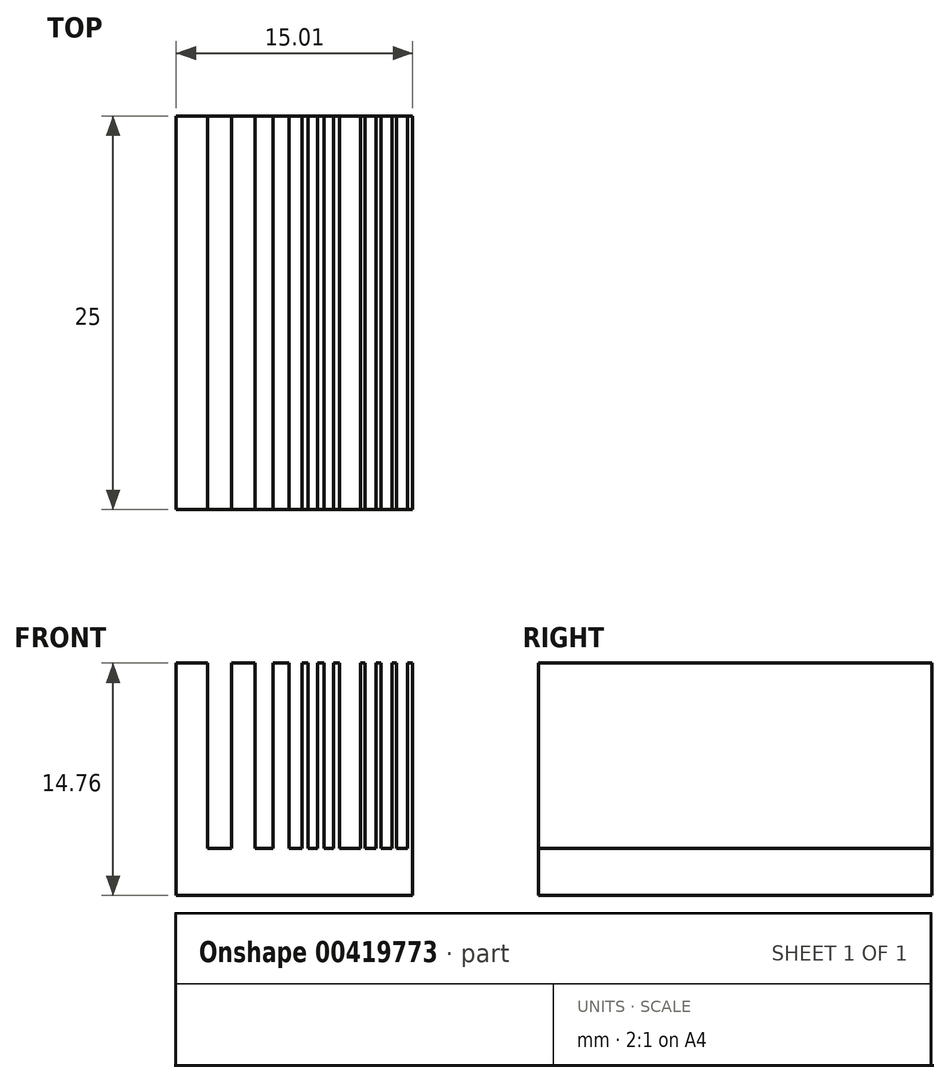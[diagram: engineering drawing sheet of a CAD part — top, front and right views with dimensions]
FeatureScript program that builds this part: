
annotation { "Feature Type Name" : "Feature", "Feature Type Description" : "" }
export const myFeature = defineFeature(function(context is Context, id is Id, definition is map)
    precondition{}
    {
        {
            var Q0;
            Q0=qCreatedBy(makeId("Front.planeOp"),FACE);
            var sketch = newSketch(context, id + "F0", { "sketchPlane" : qUnion([Q0])});
            skLineSegment(sketch, "E0.bottom", {"start": v(-44.62, -17.8) * mm, "end": v(56.98, -17.8) * mm});
            skLineSegment(sketch, "E0.top", {"start": v(-44.62, -22.89) * mm, "end": v(56.98, -22.89) * mm});
            skLineSegment(sketch, "E0.left", {"start": v(-44.62, -17.8) * mm, "end": v(-44.62, -22.89) * mm});
            skLineSegment(sketch, "E0.right", {"start": v(56.98, -17.8) * mm, "end": v(56.98, -22.89) * mm});
            skLineSegment(sketch, "E1.bottom", {"start": v(56.98, -17.8) * mm, "end": v(51.9, -17.8) * mm});
            skLineSegment(sketch, "E1.top", {"start": v(56.98, 7.6) * mm, "end": v(51.9, 7.6) * mm});
            skLineSegment(sketch, "E1.left", {"start": v(56.98, -17.8) * mm, "end": v(56.98, 7.6) * mm});
            skLineSegment(sketch, "E1.right", {"start": v(51.9, -17.8) * mm, "end": v(51.9, 7.6) * mm});
            skLineSegment(sketch, "E2.bottom", {"start": v(-44.62, -17.8) * mm, "end": v(-39.54, -17.8) * mm});
            skLineSegment(sketch, "E2.top", {"start": v(-44.62, 7.6) * mm, "end": v(-39.54, 7.6) * mm});
            skLineSegment(sketch, "E2.left", {"start": v(-44.62, -17.8) * mm, "end": v(-44.62, 7.6) * mm});
            skLineSegment(sketch, "E2.right", {"start": v(-39.54, -17.8) * mm, "end": v(-39.54, 7.6) * mm});
            skLineSegment(sketch, "E3.bottom", {"start": v(-20.37, 7.6) * mm, "end": v(-17.83, 7.6) * mm});
            skLineSegment(sketch, "E3.top", {"start": v(-20.37, -17.8) * mm, "end": v(-17.83, -17.8) * mm});
            skLineSegment(sketch, "E3.left", {"start": v(-20.37, 7.6) * mm, "end": v(-20.37, -17.8) * mm});
            skLineSegment(sketch, "E3.right", {"start": v(-17.83, 7.6) * mm, "end": v(-17.83, -17.8) * mm});
            skLineSegment(sketch, "E4.bottom", {"start": v(3.05, 7.6) * mm, "end": v(8.13, 7.6) * mm});
            skLineSegment(sketch, "E4.top", {"start": v(3.05, -17.8) * mm, "end": v(8.13, -17.8) * mm});
            skLineSegment(sketch, "E4.left", {"start": v(3.05, 7.6) * mm, "end": v(3.05, -17.8) * mm});
            skLineSegment(sketch, "E4.right", {"start": v(8.13, 7.6) * mm, "end": v(8.13, -17.8) * mm});
            skLineSegment(sketch, "E5.bottom", {"start": v(22.11, 7.6) * mm, "end": v(25.92, 7.6) * mm});
            skLineSegment(sketch, "E5.top", {"start": v(22.11, -17.8) * mm, "end": v(25.92, -17.8) * mm});
            skLineSegment(sketch, "E5.left", {"start": v(22.11, 7.6) * mm, "end": v(22.11, -17.8) * mm});
            skLineSegment(sketch, "E5.right", {"start": v(25.92, 7.6) * mm, "end": v(25.92, -17.8) * mm});
            skLineSegment(sketch, "E6.bottom", {"start": v(38.11, 7.6) * mm, "end": v(40.65, 7.6) * mm});
            skLineSegment(sketch, "E6.top", {"start": v(38.11, -17.8) * mm, "end": v(40.65, -17.8) * mm});
            skLineSegment(sketch, "E6.left", {"start": v(38.11, 7.6) * mm, "end": v(38.11, -17.8) * mm});
            skLineSegment(sketch, "E6.right", {"start": v(40.65, 7.6) * mm, "end": v(40.65, -17.8) * mm});
            skLineSegment(sketch, "E7.bottom", {"start": v(-31.28, 7.6) * mm, "end": v(-27.47, 7.6) * mm});
            skLineSegment(sketch, "E7.top", {"start": v(-31.28, -17.8) * mm, "end": v(-27.47, -17.8) * mm});
            skLineSegment(sketch, "E7.left", {"start": v(-31.28, 7.6) * mm, "end": v(-31.28, -17.8) * mm});
            skLineSegment(sketch, "E7.right", {"start": v(-27.47, 7.6) * mm, "end": v(-27.47, -17.8) * mm});
            skSolve(sketch);
        }
        {
            var Q0;
            Q0=makeQuery(id+"F0.imprint","IMPRINT",FACE,{"disambiguationData":[TD([[makeQuery(id+"F0.imprint","IMPRINT",EDGE,{"derivedFrom":sQuery(id+"F0.wireOp",EDGE,"E0.top")}),1.0]])]});
            var Q1;
            Q1=makeQuery(id+"F0.imprint","IMPRINT",FACE,{"disambiguationData":[TD([[makeQuery(id+"F0.imprint","IMPRINT",EDGE,{"derivedFrom":sQuery(id+"F0.wireOp",EDGE,"E1.bottom")}),-1.0]])]});
            var Q2;
            Q2=makeQuery(id+"F0.imprint","IMPRINT",FACE,{"disambiguationData":[TD([[makeQuery(id+"F0.imprint","IMPRINT",EDGE,{"derivedFrom":sQuery(id+"F0.wireOp",EDGE,"E6.bottom")}),-1.0]])]});
            var Q3;
            Q3=makeQuery(id+"F0.imprint","IMPRINT",FACE,{"disambiguationData":[TD([[makeQuery(id+"F0.imprint","IMPRINT",EDGE,{"derivedFrom":sQuery(id+"F0.wireOp",EDGE,"E5.bottom")}),-1.0]])]});
            var Q4;
            Q4=makeQuery(id+"F0.imprint","IMPRINT",FACE,{"disambiguationData":[TD([[makeQuery(id+"F0.imprint","IMPRINT",EDGE,{"derivedFrom":sQuery(id+"F0.wireOp",EDGE,"E4.bottom")}),-1.0]])]});
            var Q5;
            Q5=makeQuery(id+"F0.imprint","IMPRINT",FACE,{"disambiguationData":[TD([[makeQuery(id+"F0.imprint","IMPRINT",EDGE,{"derivedFrom":sQuery(id+"F0.wireOp",EDGE,"E7.bottom")}),-1.0]])]});
            var Q6;
            Q6=makeQuery(id+"F0.imprint","IMPRINT",FACE,{"disambiguationData":[TD([[makeQuery(id+"F0.imprint","IMPRINT",EDGE,{"derivedFrom":sQuery(id+"F0.wireOp",EDGE,"E2.bottom")}),1.0]])]});
            var Q7;
            Q7=makeQuery(id+"F0.imprint","IMPRINT",FACE,{"disambiguationData":[TD([[makeQuery(id+"F0.imprint","IMPRINT",EDGE,{"derivedFrom":sQuery(id+"F0.wireOp",EDGE,"E3.bottom")}),-1.0]])]});
            extrude(context, id + "F1", {"entities" : qUnion([Q0, Q1, Q2, Q3, Q4, Q5, Q6, Q7]), "depth" : 40 * mm});
        }
        {
            var Q0;
            Q0=makeQuery(id+"F1.opExtrude","SWEPT_BODY",BODY,{"disambiguationData":[OSD([sQuery(id+"F0.wireOp",EDGE,"E0.bottom"),sQuery(id+"F0.wireOp",EDGE,"E0.top"),sQuery(id+"F0.wireOp",EDGE,"E0.left"),sQuery(id+"F0.wireOp",EDGE,"E0.right"),sQuery(id+"F0.wireOp",EDGE,"E1.top"),sQuery(id+"F0.wireOp",EDGE,"E1.left"),sQuery(id+"F0.wireOp",EDGE,"E1.right"),sQuery(id+"F0.wireOp",EDGE,"E2.top"),sQuery(id+"F0.wireOp",EDGE,"E2.left"),sQuery(id+"F0.wireOp",EDGE,"E2.right"),sQuery(id+"F0.wireOp",EDGE,"E3.bottom"),sQuery(id+"F0.wireOp",EDGE,"E3.left"),sQuery(id+"F0.wireOp",EDGE,"E3.right"),sQuery(id+"F0.wireOp",EDGE,"E4.bottom"),sQuery(id+"F0.wireOp",EDGE,"E4.left"),sQuery(id+"F0.wireOp",EDGE,"E4.right"),sQuery(id+"F0.wireOp",EDGE,"E5.bottom"),sQuery(id+"F0.wireOp",EDGE,"E5.left"),sQuery(id+"F0.wireOp",EDGE,"E5.right"),sQuery(id+"F0.wireOp",EDGE,"E6.bottom"),sQuery(id+"F0.wireOp",EDGE,"E6.left"),sQuery(id+"F0.wireOp",EDGE,"E6.right"),sQuery(id+"F0.wireOp",EDGE,"E7.bottom"),sQuery(id+"F0.wireOp",EDGE,"E7.left"),sQuery(id+"F0.wireOp",EDGE,"E7.right")])]});
            deleteBodies(context, id + "F2", {"entities" : qUnion([Q0])});
        }
        {
            var Q0;
            Q0=qCreatedBy(makeId("Front.planeOp"),FACE);
            var sketch = newSketch(context, id + "F3", { "sketchPlane" : qUnion([Q0])});
            skLineSegment(sketch, "E8.bottom", {"start": v(-15.04, -11.76) * mm, "end": v(-0.04, -11.76) * mm});
            skLineSegment(sketch, "E8.top", {"start": v(-15.04, -14.76) * mm, "end": v(-0.04, -14.76) * mm});
            skLineSegment(sketch, "E8.left", {"start": v(-15.04, -11.76) * mm, "end": v(-15.04, -14.76) * mm});
            skLineSegment(sketch, "E8.right", {"start": v(-0.04, -11.76) * mm, "end": v(-0.04, -14.76) * mm});
            skLineSegment(sketch, "E9.bottom", {"start": v(-15.04, 0) * mm, "end": v(-13.04, 0) * mm});
            skLineSegment(sketch, "E9.top", {"start": v(-15.04, -11.76) * mm, "end": v(-13.04, -11.76) * mm});
            skLineSegment(sketch, "E9.left", {"start": v(-15.04, 0) * mm, "end": v(-15.04, -11.76) * mm});
            skLineSegment(sketch, "E9.right", {"start": v(-13.04, 0) * mm, "end": v(-13.04, -11.76) * mm});
            skLineSegment(sketch, "E10.bottom", {"start": v(-11.54, 0) * mm, "end": v(-10.04, 0) * mm});
            skLineSegment(sketch, "E10.top", {"start": v(-11.54, -11.76) * mm, "end": v(-10.04, -11.76) * mm});
            skLineSegment(sketch, "E10.left", {"start": v(-11.54, 0) * mm, "end": v(-11.54, -11.76) * mm});
            skLineSegment(sketch, "E10.right", {"start": v(-10.04, 0) * mm, "end": v(-10.04, -11.76) * mm});
            skLineSegment(sketch, "E11.bottom", {"start": v(-8.87, 0) * mm, "end": v(-7.87, 0) * mm});
            skLineSegment(sketch, "E11.top", {"start": v(-8.87, -11.76) * mm, "end": v(-7.87, -11.76) * mm});
            skLineSegment(sketch, "E11.left", {"start": v(-8.87, 0) * mm, "end": v(-8.87, -11.76) * mm});
            skLineSegment(sketch, "E11.right", {"start": v(-7.87, 0) * mm, "end": v(-7.87, -11.76) * mm});
            skLineSegment(sketch, "E12.bottom", {"start": v(-7.05, 0) * mm, "end": v(-6.65, 0) * mm});
            skLineSegment(sketch, "E12.top", {"start": v(-7.05, -11.76) * mm, "end": v(-6.65, -11.76) * mm});
            skLineSegment(sketch, "E12.left", {"start": v(-7.05, 0) * mm, "end": v(-7.05, -11.76) * mm});
            skLineSegment(sketch, "E12.right", {"start": v(-6.65, 0) * mm, "end": v(-6.65, -11.76) * mm});
            skLineSegment(sketch, "E13.bottom", {"start": v(-3.33, 0) * mm, "end": v(-3.03, 0) * mm});
            skLineSegment(sketch, "E13.top", {"start": v(-3.33, -11.76) * mm, "end": v(-3.03, -11.76) * mm});
            skLineSegment(sketch, "E13.left", {"start": v(-3.33, 0) * mm, "end": v(-3.33, -11.76) * mm});
            skLineSegment(sketch, "E13.right", {"start": v(-3.03, 0) * mm, "end": v(-3.03, -11.76) * mm});
            skLineSegment(sketch, "E14.1.0.0", {"start": v(-2.03, 0) * mm, "end": v(-2.03, -11.76) * mm});
            skLineSegment(sketch, "E14.1.0.1", {"start": v(-2.33, 0) * mm, "end": v(-2.33, -11.76) * mm});
            skLineSegment(sketch, "E14.1.0.2", {"start": v(-2.33, -11.76) * mm, "end": v(-2.03, -11.76) * mm});
            skLineSegment(sketch, "E14.1.0.3", {"start": v(-2.33, 0) * mm, "end": v(-2.03, 0) * mm});
            skLineSegment(sketch, "E14.2.0.0", {"start": v(-1.03, 0) * mm, "end": v(-1.03, -11.76) * mm});
            skLineSegment(sketch, "E14.2.0.1", {"start": v(-1.33, 0) * mm, "end": v(-1.33, -11.76) * mm});
            skLineSegment(sketch, "E14.2.0.2", {"start": v(-1.33, -11.76) * mm, "end": v(-1.03, -11.76) * mm});
            skLineSegment(sketch, "E14.2.0.3", {"start": v(-1.33, 0) * mm, "end": v(-1.03, 0) * mm});
            skLineSegment(sketch, "E14.direction1", {"start": v(-3.33, -11.76) * mm, "end": v(-2.33, -11.76) * mm, "construction": true});
            skLineSegment(sketch, "E15.0.3.0", {"start": v(-0.03, 0) * mm, "end": v(-0.03, -11.76) * mm});
            skLineSegment(sketch, "E15.3.3.0", {"start": v(-0.33, 0) * mm, "end": v(-0.33, -11.76) * mm});
            skLineSegment(sketch, "E15.6.3.0", {"start": v(-0.33, -11.76) * mm, "end": v(-0.03, -11.76) * mm});
            skLineSegment(sketch, "E15.9.3.0", {"start": v(-0.33, 0) * mm, "end": v(-0.03, 0) * mm});
            skLineSegment(sketch, "E16.1.0.0", {"start": v(-5.65, 0) * mm, "end": v(-5.65, -11.76) * mm});
            skLineSegment(sketch, "E16.1.0.1", {"start": v(-6.05, 0) * mm, "end": v(-6.05, -11.76) * mm});
            skLineSegment(sketch, "E16.1.0.2", {"start": v(-6.05, -11.76) * mm, "end": v(-5.65, -11.76) * mm});
            skLineSegment(sketch, "E16.1.0.3", {"start": v(-6.05, 0) * mm, "end": v(-5.65, 0) * mm});
            skLineSegment(sketch, "E16.2.0.0", {"start": v(-4.65, 0) * mm, "end": v(-4.65, -11.76) * mm});
            skLineSegment(sketch, "E16.2.0.1", {"start": v(-5.05, 0) * mm, "end": v(-5.05, -11.76) * mm});
            skLineSegment(sketch, "E16.2.0.2", {"start": v(-5.05, -11.76) * mm, "end": v(-4.65, -11.76) * mm});
            skLineSegment(sketch, "E16.2.0.3", {"start": v(-5.05, 0) * mm, "end": v(-4.65, 0) * mm});
            skLineSegment(sketch, "E16.direction1", {"start": v(-7.05, -11.76) * mm, "end": v(-6.05, -11.76) * mm, "construction": true});
            skSolve(sketch);
        }
        {
            var Q0;
            Q0=qSketchRegion(id+"F3",true);
            extrude(context, id + "F4", {"entities" : qUnion([Q0]), "depth" : 25 * mm, "symmetric" : true});
        }
    });
